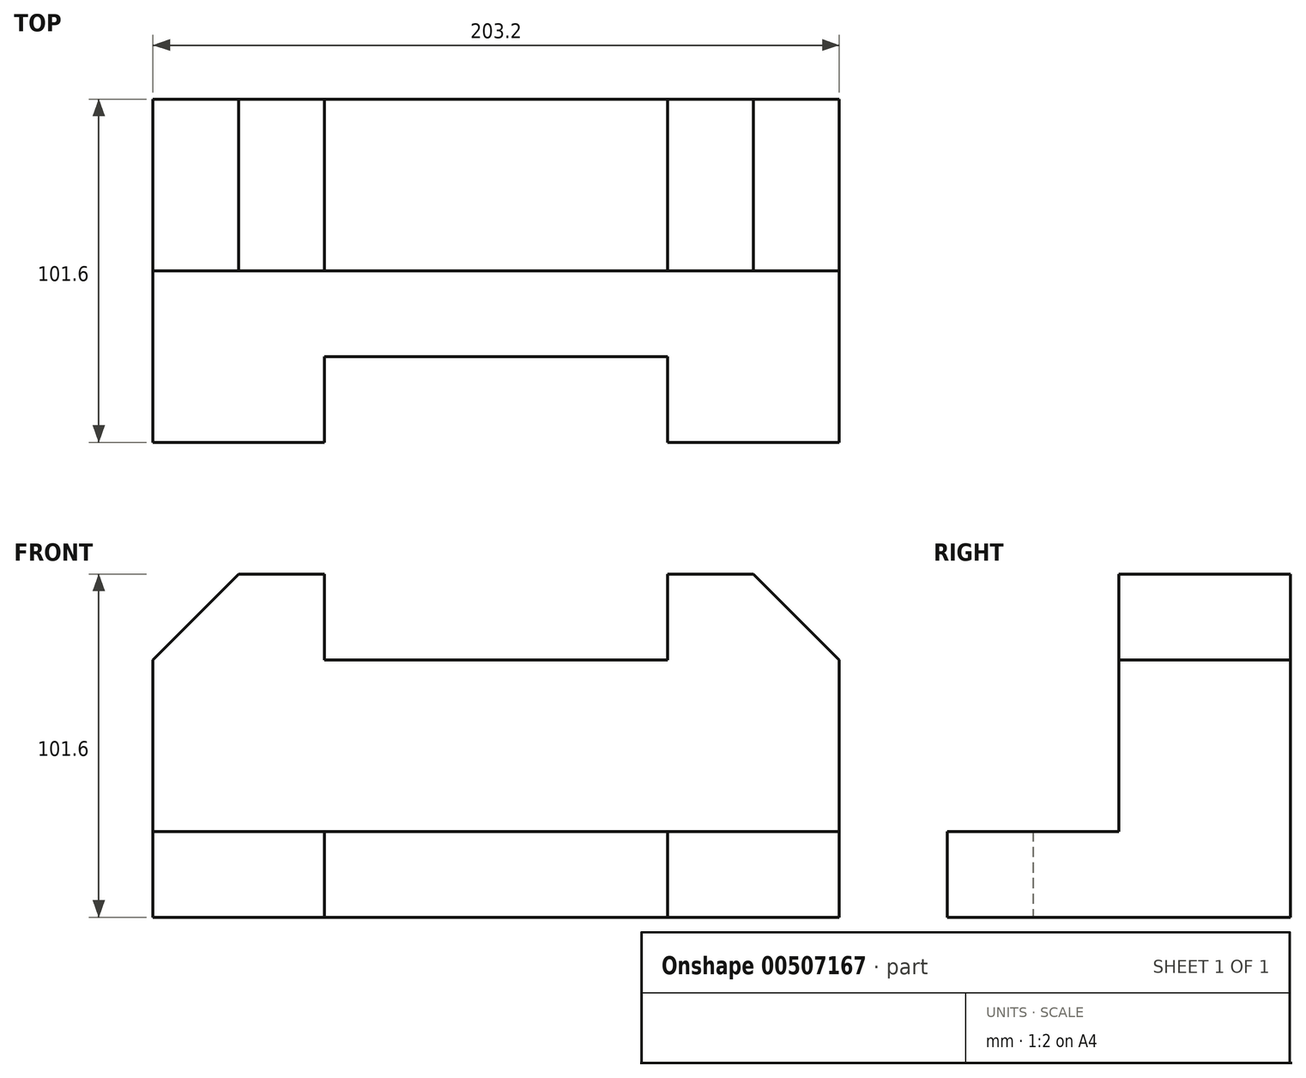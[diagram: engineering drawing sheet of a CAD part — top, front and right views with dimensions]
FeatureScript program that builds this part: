
annotation { "Feature Type Name" : "Feature", "Feature Type Description" : "" }
export const myFeature = defineFeature(function(context is Context, id is Id, definition is map)
    precondition{}
    {
        {
            var Q0;
            Q0=qCreatedBy(makeId("Front.planeOp"),FACE);
            var sketch = newSketch(context, id + "F0", { "sketchPlane" : qUnion([Q0])});
            skLineSegment(sketch, "E0.bottom", {"start": v(-101.6, 50.8) * mm, "end": v(101.6, 50.8) * mm});
            skLineSegment(sketch, "E0.top", {"start": v(-101.6, -50.8) * mm, "end": v(101.6, -50.8) * mm});
            skLineSegment(sketch, "E0.left", {"start": v(-101.6, 50.8) * mm, "end": v(-101.6, -50.8) * mm});
            skLineSegment(sketch, "E0.right", {"start": v(101.6, 50.8) * mm, "end": v(101.6, -50.8) * mm});
            skSolve(sketch);
        }
        {
            var Q0;
            Q0=qSketchRegion(id+"F0",true);
            extrude(context, id + "F1", {"entities" : qUnion([Q0]), "depth" : 101.6 * mm});
        }
        {
            var Q0;
            Q0=makeQuery(id+"F1.opExtrude","SWEPT_FACE",FACE,{"disambiguationData":[OSD([sQuery(id+"F0.wireOp",EDGE,"E0.bottom")])]});
            var sketch = newSketch(context, id + "F2", { "sketchPlane" : qUnion([Q0])});
            skLineSegment(sketch, "E1.bottom", {"start": v(-101.6, -101.6) * mm, "end": v(101.6, -101.6) * mm});
            skLineSegment(sketch, "E1.top", {"start": v(-101.6, -50.8) * mm, "end": v(101.6, -50.8) * mm});
            skLineSegment(sketch, "E1.left", {"start": v(-101.6, -101.6) * mm, "end": v(-101.6, -50.8) * mm});
            skLineSegment(sketch, "E1.right", {"start": v(101.6, -101.6) * mm, "end": v(101.6, -50.8) * mm});
            skSolve(sketch);
        }
        {
            var Q0;
            Q0 = qSketchRegion(id + "F2", true);
            extrude(context, id + "F3", {"entities" : qUnion([Q0]), "operationType" : NewBodyOperationType.REMOVE, "oppositeDirection" : true, "depth" : 76.2 * mm});
        }
        {
            var Q0;
            Q0=makeQuery(id+"F1.opExtrude","CAP_FACE",FACE,{"disambiguationData":[OSD([sQuery(id+"F0.wireOp",EDGE,"E0.bottom"),sQuery(id+"F0.wireOp",EDGE,"E0.top"),sQuery(id+"F0.wireOp",EDGE,"E0.left"),sQuery(id+"F0.wireOp",EDGE,"E0.right")])],"isStart":false});
            var sketch = newSketch(context, id + "F4", { "sketchPlane" : qUnion([Q0])});
            skLineSegment(sketch, "E2.bottom", {"start": v(-50.8, -25.4) * mm, "end": v(50.8, -25.4) * mm});
            skLineSegment(sketch, "E2.top", {"start": v(-50.8, -50.8) * mm, "end": v(50.8, -50.8) * mm});
            skLineSegment(sketch, "E2.left", {"start": v(-50.8, -25.4) * mm, "end": v(-50.8, -50.8) * mm});
            skLineSegment(sketch, "E2.right", {"start": v(50.8, -25.4) * mm, "end": v(50.8, -50.8) * mm});
            skSolve(sketch);
        }
        {
            var Q0;
            Q0 = qSketchRegion(id + "F4", true);
            extrude(context, id + "F5", {"entities" : qUnion([Q0]), "operationType" : NewBodyOperationType.REMOVE, "oppositeDirection" : true, "depth" : 25.4 * mm});
        }
        {
            var Q0;
            Q0=makeQuery(id+"F1.opExtrude","SWEPT_FACE",FACE,{"disambiguationData":[OSD([sQuery(id+"F0.wireOp",EDGE,"E0.bottom")])]});
            var sketch = newSketch(context, id + "F6", { "sketchPlane" : qUnion([Q0])});
            skLineSegment(sketch, "E3.bottom", {"start": v(-50.8, 0) * mm, "end": v(50.8, 0) * mm});
            skLineSegment(sketch, "E3.top", {"start": v(-50.8, -50.8) * mm, "end": v(50.8, -50.8) * mm});
            skLineSegment(sketch, "E3.left", {"start": v(-50.8, 0) * mm, "end": v(-50.8, -50.8) * mm});
            skLineSegment(sketch, "E3.right", {"start": v(50.8, 0) * mm, "end": v(50.8, -50.8) * mm});
            skSolve(sketch);
        }
        {
            var Q0;
            Q0 = qSketchRegion(id + "F6", true);
            extrude(context, id + "F7", {"entities" : qUnion([Q0]), "operationType" : NewBodyOperationType.REMOVE, "oppositeDirection" : true, "depth" : 25.4 * mm});
        }
        {
            var Q0;
            Q0=makeQuery(id+"F1.opExtrude","SWEPT_EDGE",EDGE,{"disambiguationData":[OSD([sQuery(id+"F0.wireOp",EDGE,"E0.bottom"),sQuery(id+"F0.wireOp",EDGE,"E0.left")])]});
            chamfer(context, id + "F8", {"entities" : qUnion([Q0]), "width" : 25.4 * mm, "tangentPropagation" : true});
        }
        {
            var Q0;
            Q0=makeQuery(id+"F1.opExtrude","SWEPT_EDGE",EDGE,{"disambiguationData":[OSD([sQuery(id+"F0.wireOp",EDGE,"E0.bottom"),sQuery(id+"F0.wireOp",EDGE,"E0.right")])]});
            chamfer(context, id + "F9", {"entities" : qUnion([Q0]), "width" : 25.4 * mm, "tangentPropagation" : true});
        }
    });
